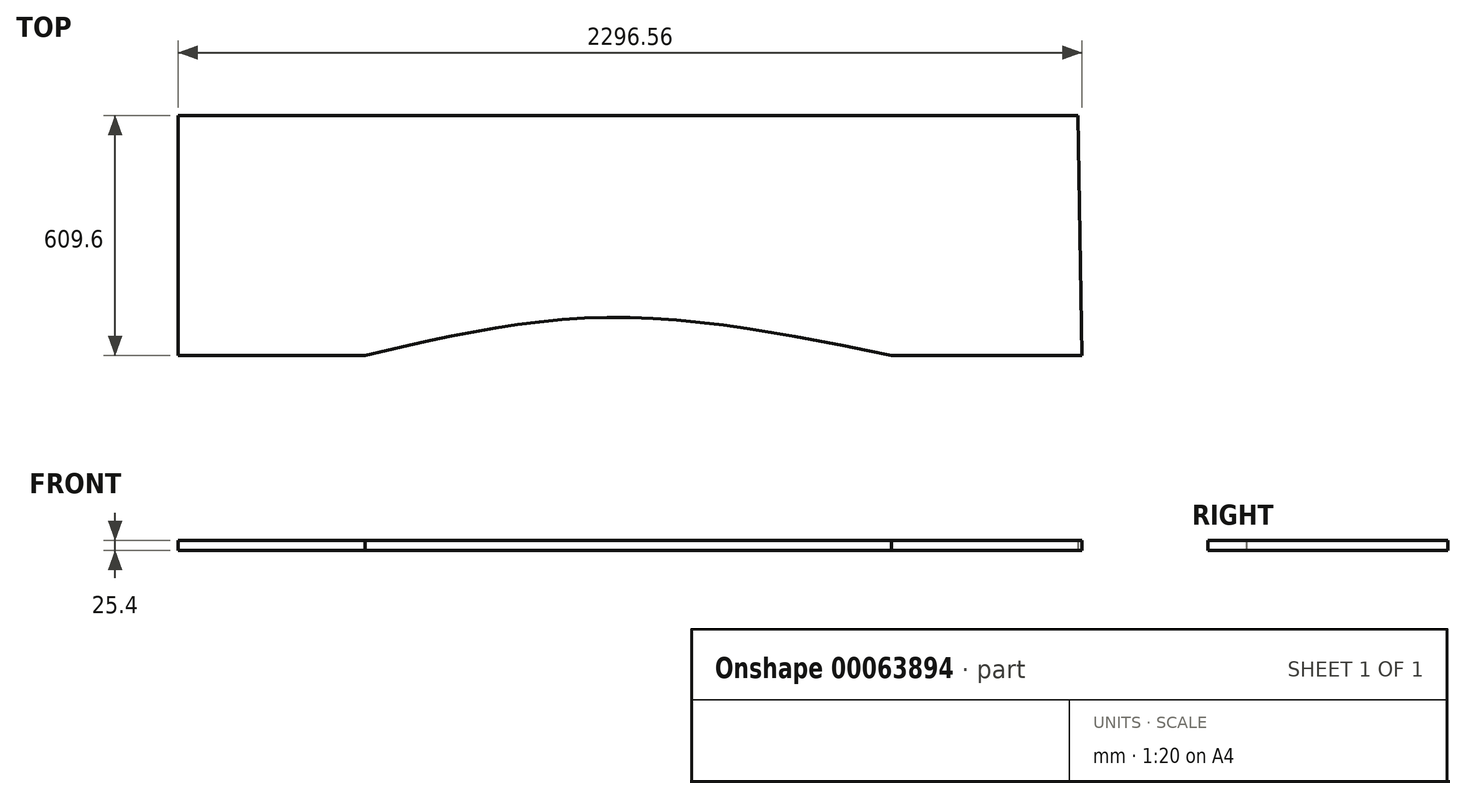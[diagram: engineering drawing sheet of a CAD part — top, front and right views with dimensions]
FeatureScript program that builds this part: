
annotation { "Feature Type Name" : "Feature", "Feature Type Description" : "" }
export const myFeature = defineFeature(function(context is Context, id is Id, definition is map)
    precondition{}
    {
        {
            var Q0;
            Q0=qCreatedBy(makeId("Top.planeOp"),FACE);
            var sketch = newSketch(context, id + "F0", { "sketchPlane" : qUnion([Q0]), "disableImprinting" : false});
            skLineSegment(sketch, "E0.top", {"start": v(-1143, 609.6) * mm, "end": v(0, 609.6) * mm});
            skLineSegment(sketch, "E0.left", {"start": v(-1143, 0) * mm, "end": v(-1143, 609.6) * mm});
            skLineSegment(sketch, "E1", {"start": v(-635, -457.2) * mm, "end": v(-635, -457.2) * mm});
            skArc(sketch, "E2", {"start": v(3.18, 177.8) * mm, "mid": v(0, 177.8) * mm, "end": v(-3.18, 177.8) * mm});
            skLineSegment(sketch, "E3.MirrorCS", {"start": v(634.96, -438.3) * mm, "end": v(634.96, -438.3) * mm});
            skLineSegment(sketch, "E4.MirrorCS", {"start": v(1135.13, -438.3) * mm, "end": v(1132.5, -438.3) * mm});
            skPoint(sketch, "E5.end.orphan", {"position": v(-585.44, -211.27) * mm});
            skPoint(sketch, "E6.MirrorCS.end.orphan", {"position": v(0, 609.6) * mm});
            skPoint(sketch, "E7.MirrorP", {"position": v(3.15, 27.88) * mm});
            skLineSegment(sketch, "E8.MirrorCS", {"start": v(1143, 609.6) * mm, "end": v(0, 609.6) * mm});
            skPoint(sketch, "E9.MirrorP", {"position": v(585.44, -211.27) * mm});
            skLineSegment(sketch, "E10", {"start": v(585.44, -211.27) * mm, "end": v(658.35, -177.84) * mm, "construction": true});
            skPoint(sketch, "E11.orphan", {"position": v(-658.35, -177.84) * mm});
            skPoint(sketch, "E12.end.orphan", {"position": v(-1143, -457.2) * mm});
            skPoint(sketch, "E13.trimOffspring.end.orphan", {"position": v(635, -457.2) * mm});
            skPoint(sketch, "E14.MirrorCS.end.orphan", {"position": v(1143, -457.2) * mm});
            skPoint(sketch, "E15.MirrorCS.start.orphan", {"position": v(1153.56, 0) * mm});
            skLineSegment(sketch, "E16", {"start": v(-1143, 0) * mm, "end": v(-668.65, 0) * mm});
            skLineSegment(sketch, "E17", {"start": v(1143, 609.6) * mm, "end": v(1153.56, 0) * mm});
            skLineSegment(sketch, "E18.trimOffspring", {"start": v(668.65, 0) * mm, "end": v(1153.56, 0) * mm});
            skFitSpline(sketch, "E19", {"points": [v(-668.65, 0) * mm, v(-47.72, 96.82) * mm, v(668.65, 0) * mm], "startDerivative": vector(1263.38, 294.22) * mm, "endDerivative": vector(1409.5, -287.44) * mm});
            skSolve(sketch);
        }
        {
            var Q0;
            Q0=makeQuery(id+"F0.imprint","IMPRINT",FACE,{"disambiguationData":[TD([[makeQuery(id+"F0.imprint","IMPRINT",EDGE,{"derivedFrom":sQuery(id+"F0.wireOp",EDGE,"E0.top")}),-1.0]])]});
            extrude(context, id + "F1", {"entities" : qUnion([Q0]), "depth" : 25.4 * mm});
        }
        {
            var Q0;
            Q0=qSketchRegion(id+"F0",true);
            extrude(context, id + "F2", {"entities" : qUnion([Q0]), "operationType" : NewBodyOperationType.ADD, "depth" : 25.4 * mm});
        }
    });
